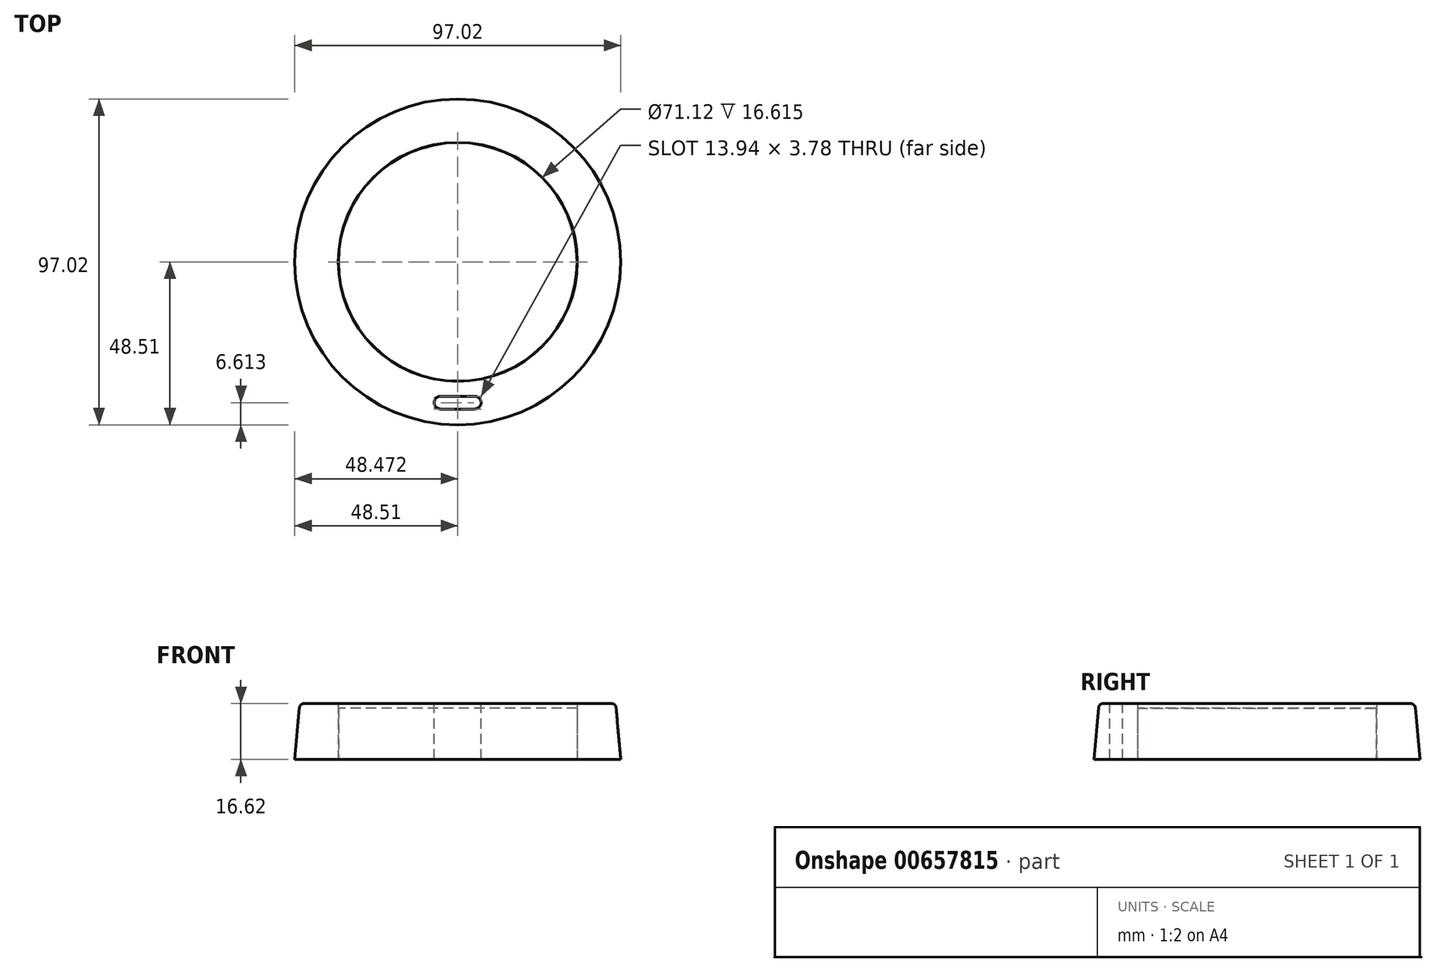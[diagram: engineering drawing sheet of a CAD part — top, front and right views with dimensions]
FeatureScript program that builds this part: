
annotation { "Feature Type Name" : "Feature", "Feature Type Description" : "" }
export const myFeature = defineFeature(function(context is Context, id is Id, definition is map)
    precondition{}
    {
        {
            var Q0;
            Q0=qCreatedBy(makeId("Front.planeOp"),FACE);
            var sketch = newSketch(context, id + "F0", { "sketchPlane" : qUnion([Q0])});
            skLineSegment(sketch, "E0", {"start": v(0, 0) * mm, "end": v(-48.5, 0) * mm});
            skLineSegment(sketch, "E1", {"start": v(-48.5, 0) * mm, "end": v(-47, 16.62) * mm});
            skLineSegment(sketch, "E2", {"start": v(-47, 16.62) * mm, "end": v(0, 16.62) * mm});
            skLineSegment(sketch, "E3", {"start": v(0, 16.62) * mm, "end": v(0, 0) * mm});
            skSolve(sketch);
        }
        {
            var Q0;
            Q0 = qSketchRegion(id + "F0", true);
            var Q1;
            Q1=sQuery(id+"F0.wireOp",EDGE,"E3");
            revolve(context, id + "F1", {"entities" : qUnion([Q0]), "axis" : qUnion([Q1]), "revolveType" : RevolveType.FULL});
        }
        {
            var Q0;
            Q0=qCreatedBy(makeId("Top.planeOp"),FACE);
            var sketch = newSketch(context, id + "F2", { "sketchPlane" : qUnion([Q0])});
            skCircle(sketch, "E4", {"center": v(0, 0) * mm, "radius": 35.56 * mm});
            skSolve(sketch);
        }
        {
            var Q0;
            Q0 = qSketchRegion(id + "F2", true);
            extrude(context, id + "F3", {"entities" : qUnion([Q0]), "operationType" : NewBodyOperationType.REMOVE, "depth" : 20.32 * mm, "offsetDistance" : 25.4 * mm});
        }
        {
            var Q0;
            Q0=qCreatedBy(makeId("Top.planeOp"),FACE);
            var sketch = newSketch(context, id + "F4", { "sketchPlane" : qUnion([Q0])});
            skCircle(sketch, "E5", {"center": v(0, 0) * mm, "radius": 35.5 * mm});
            skSolve(sketch);
        }
        {
            var Q0;
            Q0 = qSketchRegion(id + "F4", true);
            extrude(context, id + "F5", {"entities" : qUnion([Q0]), "depth" : 15.24 * mm, "offsetDistance" : 25.4 * mm});
        }
        {
            var Q0;
            Q0=qCreatedBy(makeId("Top.planeOp"),FACE);
            var sketch = newSketch(context, id + "F6", { "sketchPlane" : qUnion([Q0])});
            skLineSegment(sketch, "E6", {"start": v(-5.12, -43.79) * mm, "end": v(5.04, -43.79) * mm});
            skLineSegment(sketch, "E7", {"start": v(-5.12, -40) * mm, "end": v(5.04, -40) * mm});
            skArc(sketch, "E8", {"start": v(-5.12, -40) * mm, "mid": v(-7.01, -41.9) * mm, "end": v(-5.12, -43.79) * mm});
            skArc(sketch, "E9", {"start": v(5.04, -43.79) * mm, "mid": v(6.93, -41.9) * mm, "end": v(5.04, -40) * mm});
            skSolve(sketch);
        }
        {
            var Q0;
            Q0 = qSketchRegion(id + "F6", true);
            extrude(context, id + "F7", {"entities" : qUnion([Q0]), "operationType" : NewBodyOperationType.REMOVE, "endBound" : BoundingType.SYMMETRIC, "oppositeDirection" : true, "depth" : 147.83 * mm, "offsetDistance" : 25.4 * mm});
        }
        {
            var Q0;
            Q0=makeQuery(id+"F1.opRevolve","SWEPT_EDGE",EDGE,{"disambiguationData":[OSD([sQuery(id+"F0.wireOp",EDGE,"E1"),sQuery(id+"F0.wireOp",EDGE,"E2")])]});
            fillet(context, id + "F8", {"entities" : qUnion([Q0]), "radius" : 1.27 * mm, "tangentPropagation" : true, "allowEdgeOverflow" : false});
        }
    });
